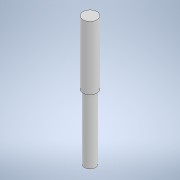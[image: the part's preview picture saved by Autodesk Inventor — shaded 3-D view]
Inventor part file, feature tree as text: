
AUTODESK INVENTOR PART (.ipt)
format: ipt  version: 2021 (Build 250183000, 183)  size: 96,256 bytes
history: native  units: mm
features: extrude x2, sketch x2
ambient origin geometry x8: Origin, YZ Plane, XZ Plane, XY Plane, X Axis, Y Axis, Z Axis, Center Point
bodies: Solid1 (feature_tree)
feature tree (4):
  extrude  "Extrusion1"  Depth=18.5mm TaperAngle=0.0deg
  extrude  "Extrusion2"  Depth=18.0mm TaperAngle=0.0deg
  sketch  "Sketch1"  dims[d0=3.2mm d1=18.5mm d2=0.0mm]
  sketch  "Sketch2"  dims[d3=4.0mm d4=18.0mm d5=0.0mm]
